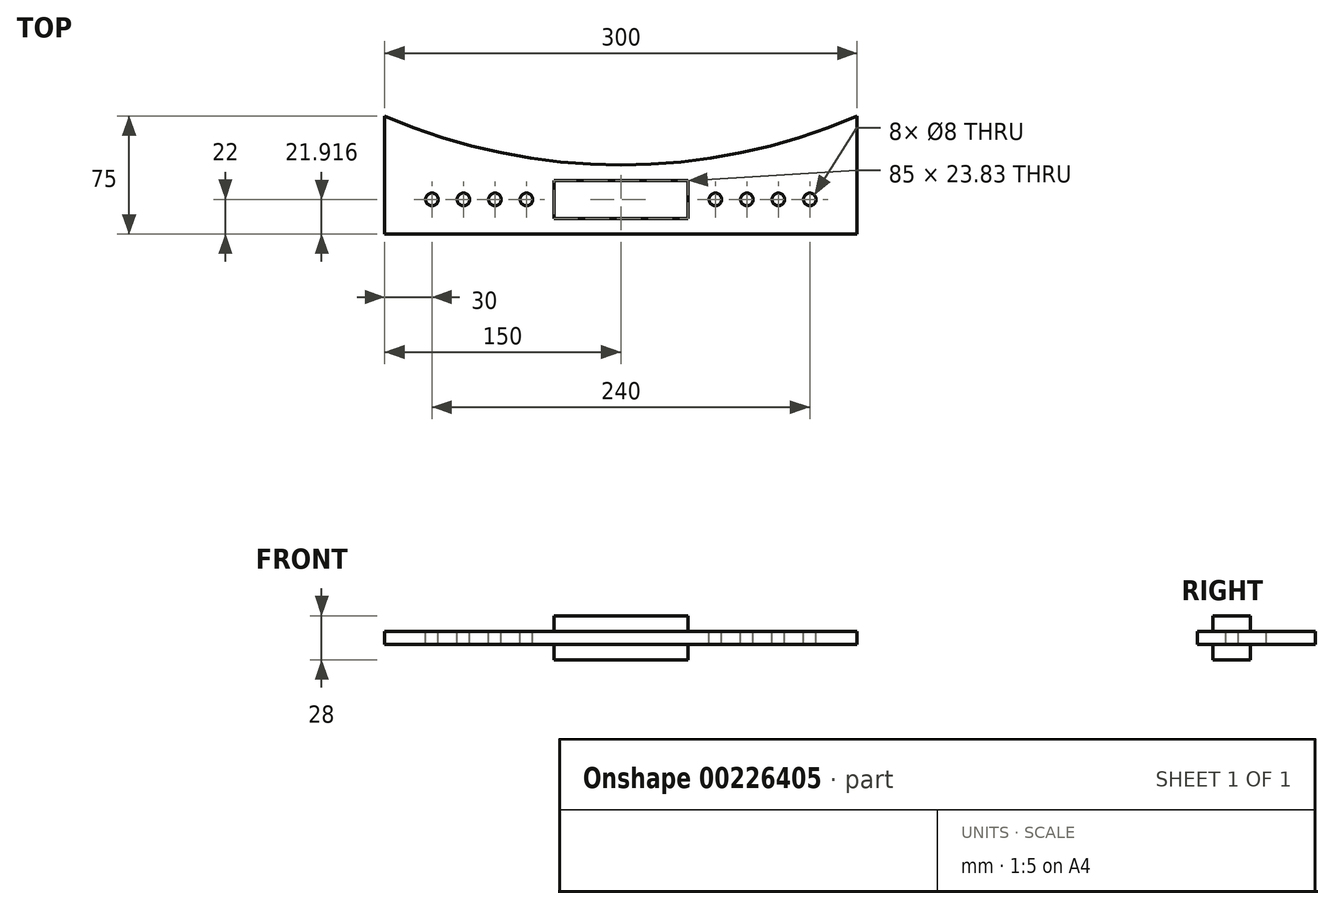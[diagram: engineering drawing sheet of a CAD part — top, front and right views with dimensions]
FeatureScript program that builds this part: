
annotation { "Feature Type Name" : "Feature", "Feature Type Description" : "" }
export const myFeature = defineFeature(function(context is Context, id is Id, definition is map)
    precondition{}
    {
        {
            var Q0;
            Q0=qCreatedBy(makeId("Front.planeOp"),FACE);
            var sketch = newSketch(context, id + "F4", { "sketchPlane" : qUnion([Q0])});
            skLineSegment(sketch, "E0.bottom", {"start": v(0, 0) * mm, "end": v(-300, 0) * mm});
            skLineSegment(sketch, "E0.top", {"start": v(0, -8) * mm, "end": v(-300, -8) * mm});
            skLineSegment(sketch, "E0.left", {"start": v(0, 0) * mm, "end": v(0, -8) * mm});
            skLineSegment(sketch, "E0.right", {"start": v(-300, 0) * mm, "end": v(-300, -8) * mm});
            skSolve(sketch);
        }
        {
            var Q0;
            Q0=makeQuery(id+"F4.imprint","IMPRINT",FACE,{"disambiguationData":[TD([[makeQuery(id+"F4.imprint","IMPRINT",EDGE,{"derivedFrom":sQuery(id+"F4.wireOp",EDGE,"E0.bottom")}),1.0]])]});
            extrude(context, id + "F0", {"entities" : qUnion([Q0]), "depth" : 75 * mm});
        }
        {
            var Q0;
            Q0=makeQuery(id+"F0.opExtrude","SWEPT_FACE",FACE,{"disambiguationData":[OSD([sQuery(id+"F4.wireOp",EDGE,"E0.bottom")])]});
            var sketch = newSketch(context, id + "F1", { "sketchPlane" : qUnion([Q0])});
            skArc(sketch, "E1", {"start": v(-300, 0) * mm, "mid": v(-150, -31.17) * mm, "end": v(0, 0) * mm});
            skSolve(sketch);
        }
        {
            var Q0;
            Q0=makeQuery(id+"F1.imprint","IMPRINT",FACE,{"disambiguationData":[TD([[makeQuery(id+"F1.imprint","IMPRINT",EDGE,{"derivedFrom":sQuery(id+"F1.wireOp",EDGE,"E1")}),1.0]])]});
            extrude(context, id + "F5", {"entities" : qUnion([Q0]), "operationType" : NewBodyOperationType.REMOVE, "oppositeDirection" : true, "depth" : 25 * mm});
        }
        {
            var Q0;
            Q0=makeQuery(id+"F0.opExtrude","SWEPT_FACE",FACE,{"disambiguationData":[OSD([sQuery(id+"F4.wireOp",EDGE,"E0.bottom")])]});
            var sketch = newSketch(context, id + "F2", { "sketchPlane" : qUnion([Q0])});
            skPoint(sketch, "E2", {"position": v(-270, -53) * mm});
            skPoint(sketch, "E3", {"position": v(-250, -53) * mm});
            skPoint(sketch, "E4", {"position": v(-230, -53) * mm});
            skPoint(sketch, "E5", {"position": v(-210, -53) * mm});
            skPoint(sketch, "E6", {"position": v(-90, -53) * mm});
            skPoint(sketch, "E7", {"position": v(-70, -53) * mm});
            skPoint(sketch, "E8", {"position": v(-50, -53) * mm});
            skPoint(sketch, "E9", {"position": v(-30, -53) * mm});
            skSolve(sketch);
        }
        {
            var Q0;
            Q0=sQuery(id+"F2.wireOp",VERTEX,"E2");
            var Q1;
            Q1=sQuery(id+"F2.wireOp",VERTEX,"E3");
            var Q2;
            Q2=sQuery(id+"F2.wireOp",VERTEX,"E4");
            var Q3;
            Q3=sQuery(id+"F2.wireOp",VERTEX,"E5");
            var Q4;
            Q4=sQuery(id+"F2.wireOp",VERTEX,"E6");
            var Q5;
            Q5=sQuery(id+"F2.wireOp",VERTEX,"E7");
            var Q6;
            Q6=sQuery(id+"F2.wireOp",VERTEX,"E8");
            var Q7;
            Q7=sQuery(id+"F2.wireOp",VERTEX,"E9");
            var Q8;
            Q8=makeQuery(id+"F0.opExtrude","SWEPT_BODY",BODY,{"disambiguationData":[OSD([sQuery(id+"F4.wireOp",EDGE,"E0.bottom"),sQuery(id+"F4.wireOp",EDGE,"E0.top"),sQuery(id+"F4.wireOp",EDGE,"E0.left"),sQuery(id+"F4.wireOp",EDGE,"E0.right")])]});
            hole(context, id + "F6", {"style" : HoleStyle.SIMPLE, "endStyle" : HoleEndStyle.THROUGH, "holeDiameter" : 8 * mm, "tappedDepth" : 12 * mm, "tapClearance" : 3, "locations" : qUnion([Q0, Q1, Q2, Q3, Q4, Q5, Q6, Q7]), "scope" : qUnion([Q8])});
        }
        {
            var Q0;
            Q0=makeQuery(id+"F0.opExtrude","SWEPT_FACE",FACE,{"disambiguationData":[OSD([sQuery(id+"F4.wireOp",EDGE,"E0.bottom")])]});
            var sketch = newSketch(context, id + "F7", { "sketchPlane" : qUnion([Q0])});
            skLineSegment(sketch, "E10.bottom", {"start": v(-107.5, -65) * mm, "end": v(-192.5, -65) * mm});
            skLineSegment(sketch, "E10.top", {"start": v(-107.5, -41.17) * mm, "end": v(-192.5, -41.17) * mm});
            skLineSegment(sketch, "E10.left", {"start": v(-107.5, -65) * mm, "end": v(-107.5, -41.17) * mm});
            skLineSegment(sketch, "E10.right", {"start": v(-192.5, -65) * mm, "end": v(-192.5, -41.17) * mm});
            skPoint(sketch, "E10.middle", {"position": v(-150, -53.08) * mm});
            skPoint(sketch, "E10.middle.positionSnap0", {"position": v(-150, -75) * mm});
            skPoint(sketch, "E10.centerSnap0", {"position": v(-150, -75) * mm});
            skSolve(sketch);
        }
        {
            var Q0;
            Q0=makeQuery(id+"F7.imprint","IMPRINT",FACE,{"disambiguationData":[TD([[makeQuery(id+"F7.imprint","IMPRINT",EDGE,{"derivedFrom":sQuery(id+"F7.wireOp",EDGE,"E10.bottom")}),-1.0]])]});
            extrude(context, id + "F3", {"entities" : qUnion([Q0]), "operationType" : NewBodyOperationType.ADD, "depth" : 10 * mm, "hasSecondDirection" : true, "secondDirectionOppositeDirection" : true, "secondDirectionDepth" : 18 * mm});
        }
    });
